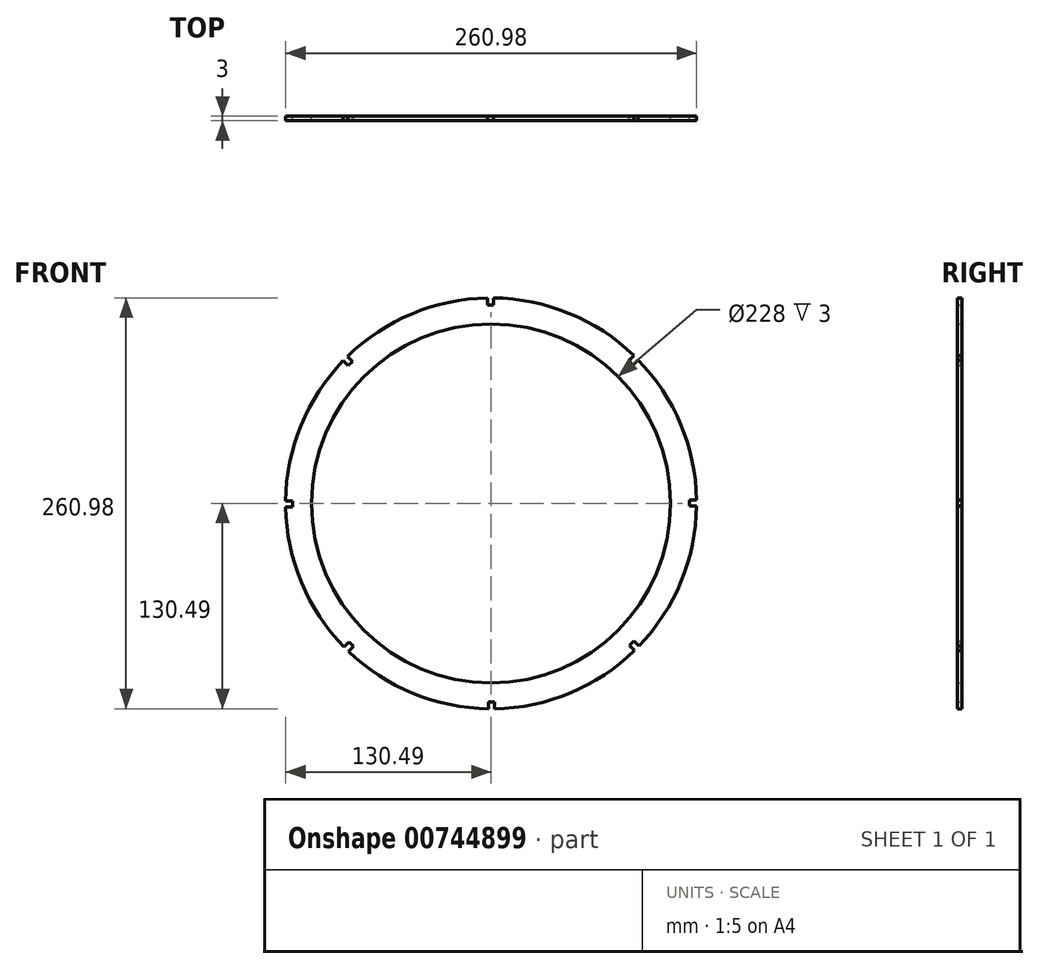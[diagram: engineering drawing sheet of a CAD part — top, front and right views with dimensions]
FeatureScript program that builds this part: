
annotation { "Feature Type Name" : "Feature", "Feature Type Description" : "" }
export const myFeature = defineFeature(function(context is Context, id is Id, definition is map)
    precondition{}
    {
        {
            var Q0;
            Q0=qCreatedBy(makeId("Front.planeOp"),FACE);
            var sketch = newSketch(context, id + "F0", { "sketchPlane" : qUnion([Q0])});
            skCircle(sketch, "E0", {"center": v(0, 0) * mm, "radius": 130.5 * mm});
            skCircle(sketch, "E1", {"center": v(0, 0) * mm, "radius": 114 * mm});
            skLineSegment(sketch, "E2.bottom", {"start": v(-2.3, 130.5) * mm, "end": v(1.5, 130.5) * mm});
            skLineSegment(sketch, "E2.top", {"start": v(-2.3, 126) * mm, "end": v(1.5, 126) * mm});
            skLineSegment(sketch, "E2.left", {"start": v(-2.3, 130.5) * mm, "end": v(-2.3, 126) * mm});
            skLineSegment(sketch, "E2.right", {"start": v(1.5, 130.5) * mm, "end": v(1.5, 126) * mm});
            skLineSegment(sketch, "E3.1.0", {"start": v(-90.72, 87.47) * mm, "end": v(-88.03, 90.16) * mm});
            skLineSegment(sketch, "E3.1.1", {"start": v(-91.22, 93.34) * mm, "end": v(-88.03, 90.16) * mm});
            skLineSegment(sketch, "E3.1.2", {"start": v(-93.9, 90.65) * mm, "end": v(-90.72, 87.47) * mm});
            skLineSegment(sketch, "E3.1.3", {"start": v(-93.9, 90.65) * mm, "end": v(-91.22, 93.34) * mm});
            skLineSegment(sketch, "E3.2.0", {"start": v(-126, -2.3) * mm, "end": v(-126, 1.5) * mm});
            skLineSegment(sketch, "E3.2.1", {"start": v(-130.5, 1.5) * mm, "end": v(-126, 1.5) * mm});
            skLineSegment(sketch, "E3.2.2", {"start": v(-130.5, -2.3) * mm, "end": v(-126, -2.3) * mm});
            skLineSegment(sketch, "E3.2.3", {"start": v(-130.5, -2.3) * mm, "end": v(-130.5, 1.5) * mm});
            skLineSegment(sketch, "E3.3.0", {"start": v(-87.47, -90.72) * mm, "end": v(-90.16, -88.03) * mm});
            skLineSegment(sketch, "E3.3.1", {"start": v(-93.34, -91.22) * mm, "end": v(-90.16, -88.03) * mm});
            skLineSegment(sketch, "E3.3.2", {"start": v(-90.65, -93.9) * mm, "end": v(-87.47, -90.72) * mm});
            skLineSegment(sketch, "E3.3.3", {"start": v(-90.65, -93.9) * mm, "end": v(-93.34, -91.22) * mm});
            skLineSegment(sketch, "E3.4.0", {"start": v(2.3, -126) * mm, "end": v(-1.5, -126) * mm});
            skLineSegment(sketch, "E3.4.1", {"start": v(-1.5, -130.5) * mm, "end": v(-1.5, -126) * mm});
            skLineSegment(sketch, "E3.4.2", {"start": v(2.3, -130.5) * mm, "end": v(2.3, -126) * mm});
            skLineSegment(sketch, "E3.4.3", {"start": v(2.3, -130.5) * mm, "end": v(-1.5, -130.5) * mm});
            skLineSegment(sketch, "E3.5.0", {"start": v(90.72, -87.47) * mm, "end": v(88.03, -90.16) * mm});
            skLineSegment(sketch, "E3.5.1", {"start": v(91.22, -93.34) * mm, "end": v(88.03, -90.16) * mm});
            skLineSegment(sketch, "E3.5.2", {"start": v(93.9, -90.65) * mm, "end": v(90.72, -87.47) * mm});
            skLineSegment(sketch, "E3.5.3", {"start": v(93.9, -90.65) * mm, "end": v(91.22, -93.34) * mm});
            skLineSegment(sketch, "E3.6.0", {"start": v(126, 2.3) * mm, "end": v(126, -1.5) * mm});
            skLineSegment(sketch, "E3.6.1", {"start": v(130.5, -1.5) * mm, "end": v(126, -1.5) * mm});
            skLineSegment(sketch, "E3.6.2", {"start": v(130.5, 2.3) * mm, "end": v(126, 2.3) * mm});
            skLineSegment(sketch, "E3.6.3", {"start": v(130.5, 2.3) * mm, "end": v(130.5, -1.5) * mm});
            skLineSegment(sketch, "E3.7.0", {"start": v(87.47, 90.72) * mm, "end": v(90.16, 88.03) * mm});
            skLineSegment(sketch, "E3.7.1", {"start": v(93.34, 91.22) * mm, "end": v(90.16, 88.03) * mm});
            skLineSegment(sketch, "E3.7.2", {"start": v(90.65, 93.9) * mm, "end": v(87.47, 90.72) * mm});
            skLineSegment(sketch, "E3.7.3", {"start": v(90.65, 93.9) * mm, "end": v(93.34, 91.22) * mm});
            skSolve(sketch);
        }
        {
            var Q0;
            Q0=makeQuery(id+"F0.imprint","IMPRINT",FACE,{"disambiguationData":[TD([[makeQuery(id+"F0.imprint","IMPRINT",EDGE,{"derivedFrom":sQuery(id+"F0.wireOp",EDGE,"E1")}),-1.0]])]});
            extrude(context, id + "F1", {"entities" : qUnion([Q0]), "depth" : 3 * mm, "offsetDistance" : 25 * mm});
        }
    });
